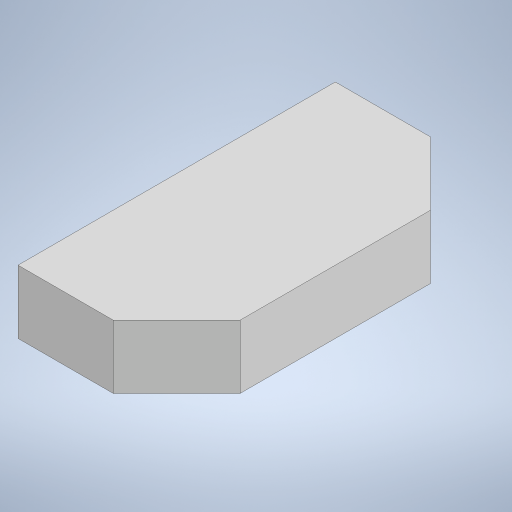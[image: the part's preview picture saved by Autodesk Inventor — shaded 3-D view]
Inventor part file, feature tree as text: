
AUTODESK INVENTOR PART (.ipt)
format: ipt  version: 2023 (Build 270158000, 158)  size: 219,136 bytes
history: native  units: mm
features: extrude x3, sketch x3, other x1, chamfer x1
ambient origin geometry x8: Origin, YZ Plane, XZ Plane, XY Plane, X Axis, Y Axis, Z Axis, Center Point
bodies: Body1 (feature_tree)
feature tree (8):
  other  "솔리드1"
  extrude  "돌출1"  Depth=50.0mm
  chamfer  "모따기1"  Distance=25.0mm
  extrude  "돌출2"  Depth=10.0mm TaperAngle=0.0deg
  extrude  "돌출3"  Depth=10.0mm TaperAngle=45.0deg
  sketch  "스케치1"
  sketch  "스케치2"
  sketch  "스케치3"
